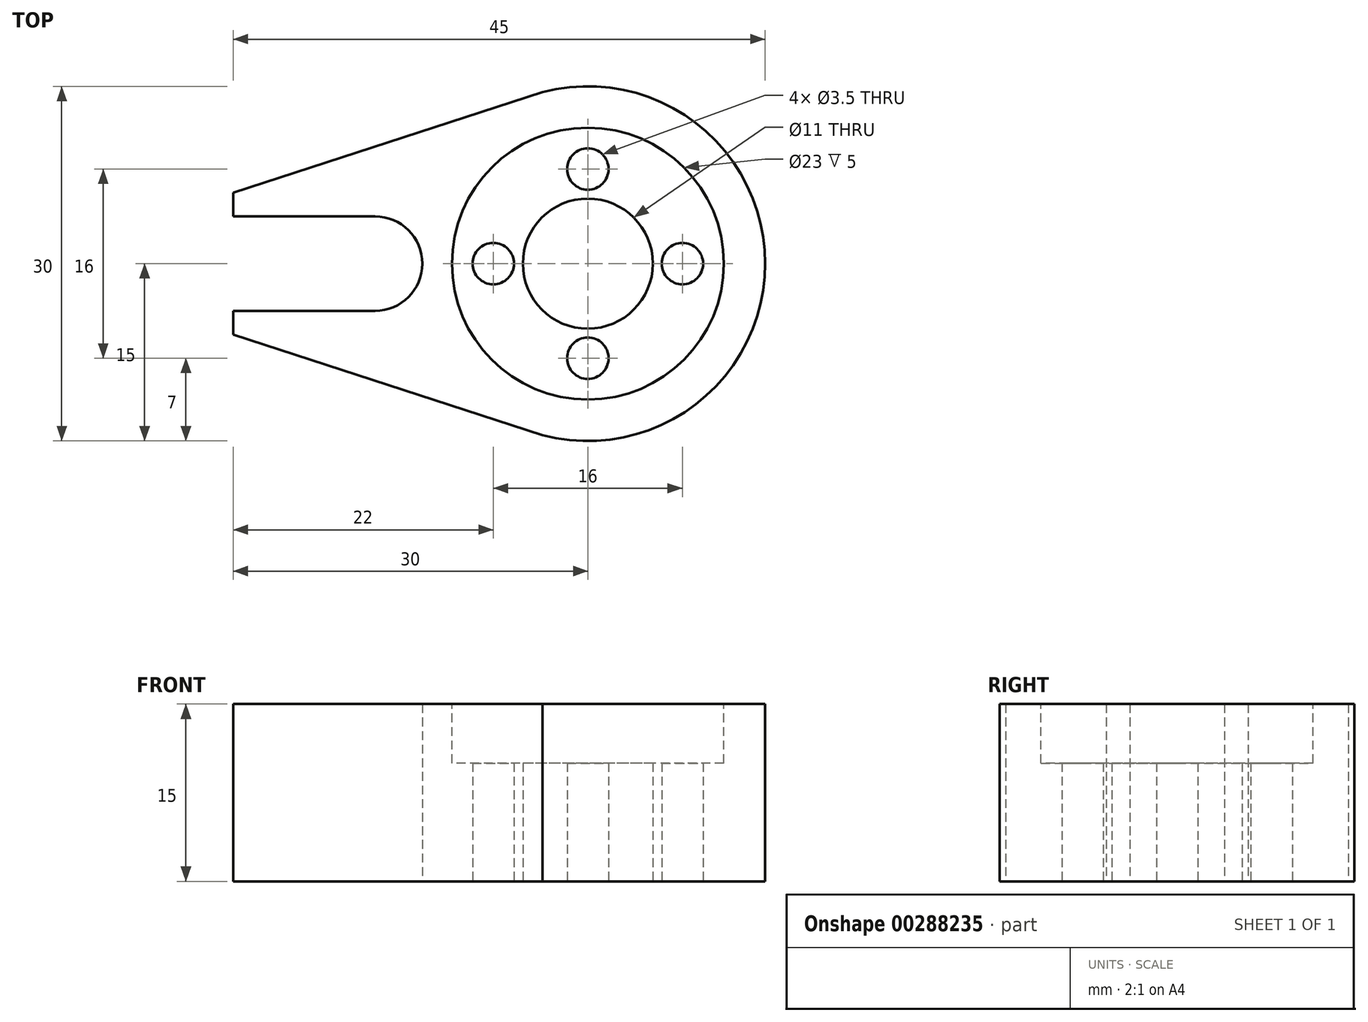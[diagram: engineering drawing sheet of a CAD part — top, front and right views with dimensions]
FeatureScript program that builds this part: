
annotation { "Feature Type Name" : "Feature", "Feature Type Description" : "" }
export const myFeature = defineFeature(function(context is Context, id is Id, definition is map)
    precondition{}
    {
        {
            var Q0;
            Q0=qCreatedBy(makeId("Top.planeOp"),FACE);
            var sketch = newSketch(context, id + "F0", { "sketchPlane" : qUnion([Q0])});
            skCircle(sketch, "E0", {"center": v(0, 0) * mm, "radius": 5.5 * mm});
            skArc(sketch, "E1", {"start": v(-18, -4) * mm, "mid": v(-14, 0) * mm, "end": v(-18, 4) * mm});
            skArc(sketch, "E2", {"start": v(-3.84, -14.5) * mm, "mid": v(15, 0) * mm, "end": v(-3.84, 14.5) * mm});
            skLineSegment(sketch, "E3", {"start": v(-3.84, 14.5) * mm, "end": v(-30, 6) * mm});
            skLineSegment(sketch, "E4", {"start": v(-30, 6) * mm, "end": v(-30, 4) * mm});
            skLineSegment(sketch, "E5", {"start": v(-18, 4) * mm, "end": v(-30, 4) * mm});
            skLineSegment(sketch, "E6.MirrorCS", {"start": v(-18, -4) * mm, "end": v(-30, -4) * mm});
            skLineSegment(sketch, "E7.MirrorCS", {"start": v(-3.84, -14.5) * mm, "end": v(-30, -6) * mm});
            skLineSegment(sketch, "E8.MirrorCS", {"start": v(-30, -6) * mm, "end": v(-30, -4) * mm});
            skSolve(sketch);
        }
        {
            var Q0;
            Q0=makeQuery(id+"F0.imprint","IMPRINT",FACE,{"disambiguationData":[TD([[makeQuery(id+"F0.imprint","IMPRINT",EDGE,{"derivedFrom":sQuery(id+"F0.wireOp",EDGE,"E0")}),-1.0]])]});
            extrude(context, id + "F1", {"entities" : qUnion([Q0]), "depth" : 15 * mm});
        }
        {
            var Q0;
            Q0=makeQuery(id+"F1.opExtrude","CAP_FACE",FACE,{"disambiguationData":[OSD([sQuery(id+"F0.wireOp",EDGE,"E0"),sQuery(id+"F0.wireOp",EDGE,"E1"),sQuery(id+"F0.wireOp",EDGE,"E2"),sQuery(id+"F0.wireOp",EDGE,"E3"),sQuery(id+"F0.wireOp",EDGE,"E4"),sQuery(id+"F0.wireOp",EDGE,"E5"),sQuery(id+"F0.wireOp",EDGE,"E6.MirrorCS"),sQuery(id+"F0.wireOp",EDGE,"E7.MirrorCS"),sQuery(id+"F0.wireOp",EDGE,"E8.MirrorCS")])],"isStart":false});
            var sketch = newSketch(context, id + "F2", { "sketchPlane" : qUnion([Q0])});
            skCircle(sketch, "E9", {"center": v(0, 0) * mm, "radius": 11.5 * mm});
            skSolve(sketch);
        }
        {
            var Q0;
            Q0=qSketchRegion(id+"F2",true);
            extrude(context, id + "F3", {"entities" : qUnion([Q0]), "operationType" : NewBodyOperationType.REMOVE, "oppositeDirection" : true, "depth" : 5 * mm});
        }
        {
            var Q0;
            Q0=makeQuery(id+"F3.boolean.opBoolean","COPY",FACE,{"derivedFrom":makeQuery(id+"F3.opExtrude","CAP_FACE",FACE,{"disambiguationData":[OSD([sQuery(id+"F2.wireOp",EDGE,"E9")])],"isStart":false})});
            var sketch = newSketch(context, id + "F4", { "sketchPlane" : qUnion([Q0])});
            skPoint(sketch, "E10", {"position": v(0, 8) * mm});
            skPoint(sketch, "E11.1.0", {"position": v(-8, 0) * mm});
            skPoint(sketch, "E11.2.0", {"position": v(0, -8) * mm});
            skPoint(sketch, "E11.3.0", {"position": v(8, 0) * mm});
            skPoint(sketch, "E11.center", {"position": v(0, 0) * mm});
            skSolve(sketch);
        }
        {
            var Q0;
            Q0=sQuery(id+"F4.wireOp",VERTEX,"E10");
            var Q1;
            Q1=sQuery(id+"F4.wireOp",VERTEX,"E11.3.0");
            var Q2;
            Q2=sQuery(id+"F4.wireOp",VERTEX,"E11.2.0");
            var Q3;
            Q3=sQuery(id+"F4.wireOp",VERTEX,"E11.1.0");
            var Q4;
            Q4=makeQuery(id+"F1.opExtrude","SWEPT_BODY",BODY,{"disambiguationData":[OSD([sQuery(id+"F0.wireOp",EDGE,"E0"),sQuery(id+"F0.wireOp",EDGE,"E1"),sQuery(id+"F0.wireOp",EDGE,"E2"),sQuery(id+"F0.wireOp",EDGE,"E3"),sQuery(id+"F0.wireOp",EDGE,"E4"),sQuery(id+"F0.wireOp",EDGE,"E5"),sQuery(id+"F0.wireOp",EDGE,"E6.MirrorCS"),sQuery(id+"F0.wireOp",EDGE,"E7.MirrorCS"),sQuery(id+"F0.wireOp",EDGE,"E8.MirrorCS")])]});
            hole(context, id + "F5", {"style" : HoleStyle.SIMPLE, "endStyle" : HoleEndStyle.THROUGH, "holeDiameter" : 3.5 * mm, "tappedDepth" : 12 * mm, "tapClearance" : 3, "startFromSketch" : true, "locations" : qUnion([Q0, Q1, Q2, Q3]), "scope" : qUnion([Q4])});
        }
    });
